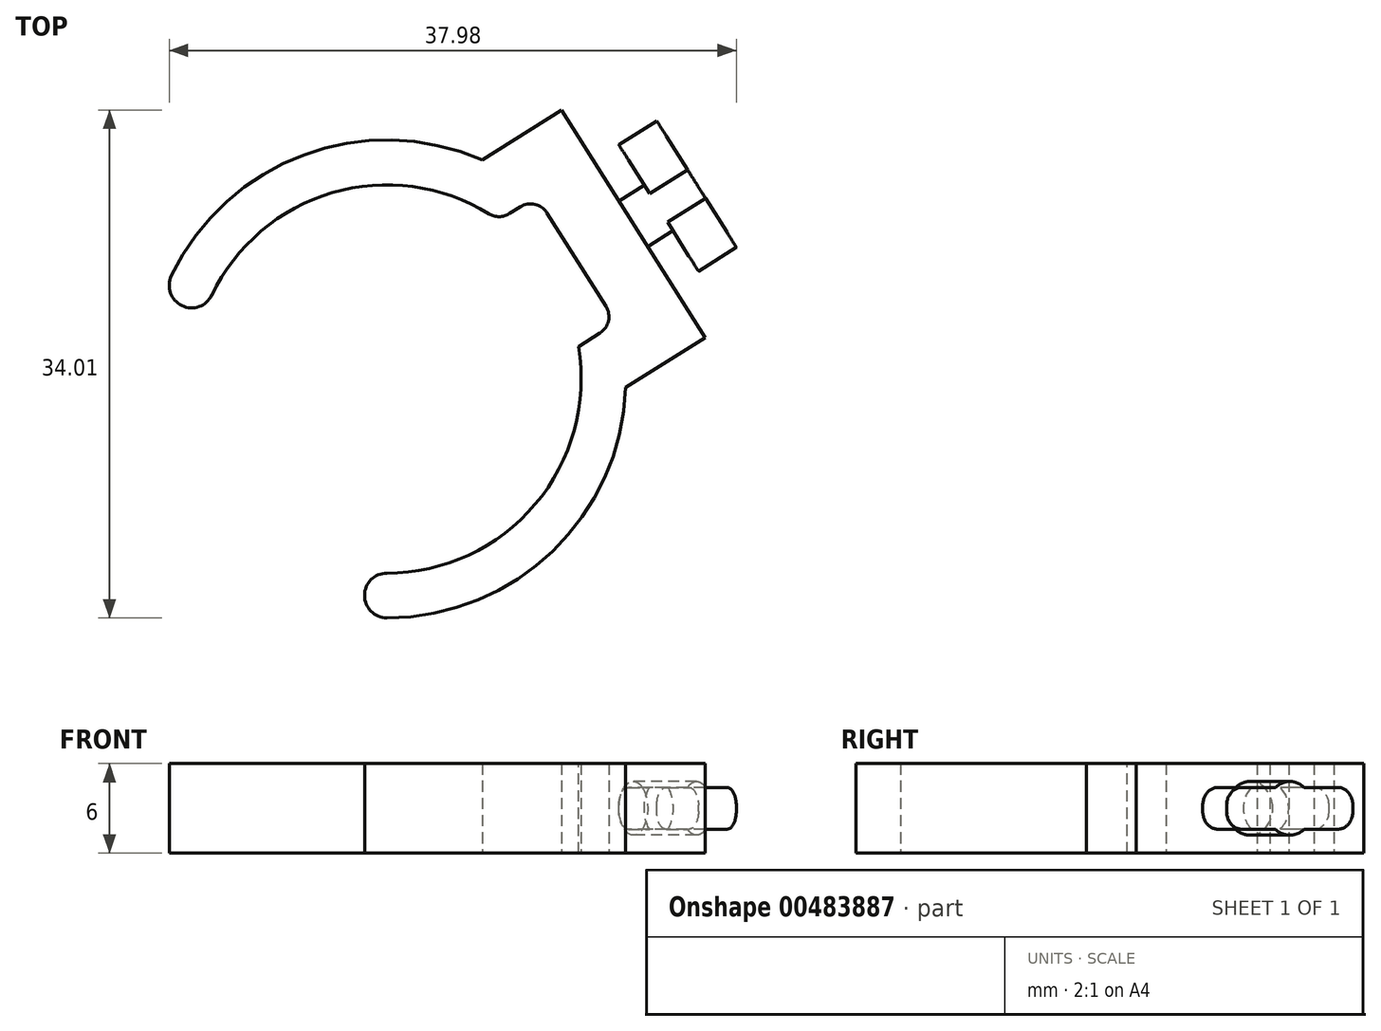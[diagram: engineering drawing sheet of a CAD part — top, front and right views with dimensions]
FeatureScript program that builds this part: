
annotation { "Feature Type Name" : "Feature", "Feature Type Description" : "" }
export const myFeature = defineFeature(function(context is Context, id is Id, definition is map)
    precondition{}
    {
        {
            var Q0;
            Q0=qCreatedBy(makeId("Top.planeOp"),FACE);
            var sketch = newSketch(context, id + "F0", { "sketchPlane" : qUnion([Q0])});
            skArc(sketch, "E0", {"start": v(0, -13) * mm, "mid": v(11, 6.93) * mm, "end": v(-11.72, 5.62) * mm});
            skArc(sketch, "E1.0", {"start": v(0, -16) * mm, "mid": v(13.54, 8.53) * mm, "end": v(-14.43, 6.91) * mm});
            skArc(sketch, "E2", {"start": v(-14.43, 6.91) * mm, "mid": v(-13.73, 4.91) * mm, "end": v(-11.72, 5.62) * mm});
            skArc(sketch, "E3", {"start": v(0, -13) * mm, "mid": v(-1.5, -14.5) * mm, "end": v(0, -16) * mm});
            skLineSegment(sketch, "E4", {"start": v(11, 6.93) * mm, "end": v(15.8, -0.69) * mm});
            skLineSegment(sketch, "E5", {"start": v(15.8, -0.69) * mm, "end": v(21.3, 2.78) * mm});
            skLineSegment(sketch, "E6", {"start": v(21.3, 2.78) * mm, "end": v(11.7, 18) * mm});
            skLineSegment(sketch, "E7", {"start": v(11.7, 18) * mm, "end": v(6.2, 14.54) * mm});
            skLineSegment(sketch, "E8", {"start": v(6.2, 14.54) * mm, "end": v(11, 6.93) * mm});
            skSolve(sketch);
        }
        {
            var Q0;
            {var subQ0=sQuery(id+"F0.wireOp",EDGE,"E3");Q0=makeQuery(id+"F0.imprint","IMPRINT",FACE,{"disambiguationData":[TD([[makeQuery(id+"F0.imprint","IMPRINT",EDGE,{"derivedFrom":subQ0}),1.0]])]});}
            var Q1;
            {var subQ0=sQuery(id+"F0.wireOp",EDGE,"E2");Q1=makeQuery(id+"F0.imprint","IMPRINT",FACE,{"disambiguationData":[TD([[makeQuery(id+"F0.imprint","IMPRINT",EDGE,{"derivedFrom":subQ0}),1.0]])]});}
            var Q2;
            {var subQ0=sQuery(id+"F0.wireOp",EDGE,"E4");var subQ1=sQuery(id+"F0.wireOp",EDGE,"E1.0");var subQ2=makeQuery(id+"F0.imprint","INTERSECT",VERTEX,{"derivedFrom":[subQ1,subQ0]});Q2=makeQuery(id+"F0.imprint","IMPRINT",FACE,{"disambiguationData":[TD([[makeQuery(id+"F0.imprint","IMPRINT",EDGE,{"disambiguationData":[TD([[subQ2,-1.0]])],"derivedFrom":subQ1}),1.0]])]});}
            var Q3;
            {var subQ0=sQuery(id+"F0.wireOp",EDGE,"E5");Q3=makeQuery(id+"F0.imprint","IMPRINT",FACE,{"disambiguationData":[TD([[makeQuery(id+"F0.imprint","IMPRINT",EDGE,{"derivedFrom":subQ0}),1.0]])]});}
            extrude(context, id + "F1", {"entities" : qUnion([Q0, Q1, Q2, Q3]), "depth" : 6 * mm});
        }
        {
            var Q0;
            Q0=makeQuery(id+"F1.opExtrude","SWEPT_FACE",FACE,{"disambiguationData":[OSD([sQuery(id+"F0.wireOp",EDGE,"E6")])]});
            var sketch = newSketch(context, id + "F2", { "sketchPlane" : qUnion([Q0])});
            skCircle(sketch, "E9", {"center": v(0, 3) * mm, "radius": 1.8 * mm});
            skSolve(sketch);
        }
        {
            var Q0;
            Q0=makeQuery(id+"F2.imprint","IMPRINT",FACE,{"disambiguationData":[TD([[makeQuery(id+"F2.imprint","IMPRINT",EDGE,{"derivedFrom":sQuery(id+"F2.wireOp",EDGE,"E9")}),1.0]])]});
            extrude(context, id + "F3", {"entities" : qUnion([Q0]), "operationType" : NewBodyOperationType.ADD, "depth" : 2 * mm});
        }
        {
            var Q0;
            Q0=makeQuery(id+"F3.opExtrude","CAP_FACE",FACE,{"disambiguationData":[OSD([sQuery(id+"F2.wireOp",EDGE,"E9")])],"isStart":false});
            var sketch = newSketch(context, id + "F4", { "sketchPlane" : qUnion([Q0])});
            skLineSegment(sketch, "E10.bottom", {"start": v(5, 1.6) * mm, "end": v(-5, 1.6) * mm});
            skLineSegment(sketch, "E10.top", {"start": v(5, 4.4) * mm, "end": v(-5, 4.4) * mm});
            skLineSegment(sketch, "E10.left", {"start": v(5, 1.6) * mm, "end": v(5, 4.4) * mm});
            skLineSegment(sketch, "E10.right", {"start": v(-5, 1.6) * mm, "end": v(-5, 4.4) * mm});
            skPoint(sketch, "E10.middle", {"position": v(0, 3) * mm});
            skSolve(sketch);
        }
        {
            var Q0;
            {var subQ0=sQuery(id+"F4.wireOp",EDGE,"E10.top");var subQ1=makeQuery(id+"F3.opExtrude","CAP_EDGE",EDGE,{"disambiguationData":[OSD([sQuery(id+"F2.wireOp",EDGE,"E9")])],"isStart":false});var subQ2=makeQuery(id+"F4.imprint","INTERSECT",VERTEX,{"disambiguationData":[OD(0.0)],"derivedFrom":[subQ1,subQ0]});Q0=makeQuery(id+"F4.imprint","IMPRINT",FACE,{"disambiguationData":[TD([[makeQuery(id+"F4.imprint","IMPRINT",EDGE,{"disambiguationData":[TD([[subQ2,-1.0]])],"derivedFrom":subQ0}),-1.0]])]});}
            var Q1;
            {var subQ0=sQuery(id+"F4.wireOp",EDGE,"E10.bottom");var subQ1=makeQuery(id+"F3.opExtrude","CAP_EDGE",EDGE,{"disambiguationData":[OSD([sQuery(id+"F2.wireOp",EDGE,"E9")])],"isStart":false});var subQ2=makeQuery(id+"F4.imprint","INTERSECT",VERTEX,{"disambiguationData":[OD(0.0)],"derivedFrom":[subQ1,subQ0]});Q1=makeQuery(id+"F4.imprint","IMPRINT",FACE,{"disambiguationData":[TD([[makeQuery(id+"F4.imprint","IMPRINT",EDGE,{"disambiguationData":[TD([[subQ2,-1.0]])],"derivedFrom":subQ0}),-1.0]])]});}
            var Q2;
            {var subQ0=sQuery(id+"F4.wireOp",EDGE,"E10.left");Q2=makeQuery(id+"F4.imprint","IMPRINT",FACE,{"disambiguationData":[TD([[makeQuery(id+"F4.imprint","IMPRINT",EDGE,{"derivedFrom":subQ0}),1.0]])]});}
            var Q3;
            {var subQ0=sQuery(id+"F4.wireOp",EDGE,"E10.right");Q3=makeQuery(id+"F4.imprint","IMPRINT",FACE,{"disambiguationData":[TD([[makeQuery(id+"F4.imprint","IMPRINT",EDGE,{"derivedFrom":subQ0}),-1.0]])]});}
            var Q4;
            {var subQ0=sQuery(id+"F4.wireOp",EDGE,"E10.bottom");var subQ1=makeQuery(id+"F3.opExtrude","CAP_EDGE",EDGE,{"disambiguationData":[OSD([sQuery(id+"F2.wireOp",EDGE,"E9")])],"isStart":false});var subQ2=makeQuery(id+"F4.imprint","INTERSECT",VERTEX,{"disambiguationData":[OD(0.0)],"derivedFrom":[subQ1,subQ0]});Q4=makeQuery(id+"F4.imprint","IMPRINT",FACE,{"disambiguationData":[TD([[makeQuery(id+"F4.imprint","IMPRINT",EDGE,{"disambiguationData":[TD([[subQ2,-1.0]])],"derivedFrom":subQ0}),1.0]])]});}
            extrude(context, id + "F5", {"entities" : qUnion([Q0, Q1, Q2, Q3, Q4]), "operationType" : NewBodyOperationType.ADD, "depth" : 3 * mm});
        }
        {
            var Q0;
            Q0=makeQuery(id+"F5.opExtrude","SWEPT_EDGE",EDGE,{"disambiguationData":[OSD([sQuery(id+"F4.wireOp",EDGE,"E10.top"),sQuery(id+"F4.wireOp",EDGE,"E10.right")])]});
            var Q1;
            Q1=makeQuery(id+"F5.opExtrude","SWEPT_EDGE",EDGE,{"disambiguationData":[OSD([sQuery(id+"F4.wireOp",EDGE,"E10.bottom"),sQuery(id+"F4.wireOp",EDGE,"E10.right")])]});
            var Q2;
            Q2=makeQuery(id+"F5.opExtrude","SWEPT_EDGE",EDGE,{"disambiguationData":[OSD([sQuery(id+"F4.wireOp",EDGE,"E10.top"),sQuery(id+"F4.wireOp",EDGE,"E10.left")])]});
            var Q3;
            Q3=makeQuery(id+"F5.opExtrude","SWEPT_EDGE",EDGE,{"disambiguationData":[OSD([sQuery(id+"F4.wireOp",EDGE,"E10.bottom"),sQuery(id+"F4.wireOp",EDGE,"E10.left")])]});
            fillet(context, id + "F6", {"entities" : qUnion([Q0, Q1, Q2, Q3]), "radius" : 1.2 * mm, "tangentPropagation" : true, "allowEdgeOverflow" : false});
        }
        {
            var Q0;
            Q0=makeQuery(id+"F1.opExtrude","CAP_FACE",FACE,{"disambiguationData":[OSD([sQuery(id+"F0.wireOp",EDGE,"E0"),sQuery(id+"F0.wireOp",EDGE,"E1.0"),sQuery(id+"F0.wireOp",EDGE,"E2"),sQuery(id+"F0.wireOp",EDGE,"E3"),sQuery(id+"F0.wireOp",EDGE,"E4"),sQuery(id+"F0.wireOp",EDGE,"E5"),sQuery(id+"F0.wireOp",EDGE,"E6"),sQuery(id+"F0.wireOp",EDGE,"E7"),sQuery(id+"F0.wireOp",EDGE,"E8")])],"isStart":false});
            var sketch = newSketch(context, id + "F7", { "sketchPlane" : qUnion([Q0])});
            skLineSegment(sketch, "E11", {"start": v(16.5, 10.4) * mm, "end": v(11, 6.93) * mm, "construction": true});
            skLineSegment(sketch, "E12", {"start": v(11, 6.93) * mm, "end": v(12.7, 8) * mm});
            skLineSegment(sketch, "E13", {"start": v(12.7, 8) * mm, "end": v(15.36, 3.76) * mm});
            skLineSegment(sketch, "E14", {"start": v(15.36, 3.76) * mm, "end": v(11.97, 1.63) * mm});
            skLineSegment(sketch, "E15", {"start": v(11.97, 1.63) * mm, "end": v(6.64, 10.1) * mm});
            skLineSegment(sketch, "E16", {"start": v(6.64, 10.1) * mm, "end": v(10.03, 12.22) * mm});
            skLineSegment(sketch, "E17", {"start": v(10.03, 12.22) * mm, "end": v(12.7, 8) * mm});
            skSolve(sketch);
        }
        {
            var Q0;
            {var subQ0=sQuery(id+"F7.wireOp",EDGE,"E12");Q0=makeQuery(id+"F7.imprint","IMPRINT",FACE,{"disambiguationData":[TD([[makeQuery(id+"F7.imprint","IMPRINT",EDGE,{"derivedFrom":subQ0}),1.0]])]});}
            var Q1;
            {var subQ0=sQuery(id+"F7.wireOp",EDGE,"E12");Q1=makeQuery(id+"F7.imprint","IMPRINT",FACE,{"disambiguationData":[TD([[makeQuery(id+"F7.imprint","IMPRINT",EDGE,{"derivedFrom":subQ0}),-1.0]])]});}
            extrude(context, id + "F8", {"entities" : qUnion([Q0, Q1]), "operationType" : NewBodyOperationType.REMOVE, "oppositeDirection" : true, "depth" : 6.1 * mm});
        }
        {
            var Q0;
            Q0=makeQuery(id+"F8.boolean.opBoolean","COPY",EDGE,{"derivedFrom":makeQuery(id+"F8.opExtrude","SWEPT_EDGE",EDGE,{"disambiguationData":[OSD([sQuery(id+"F0.wireOp",EDGE,"E0"),sQuery(id+"F7.wireOp",EDGE,"E16")])]})});
            var Q1;
            Q1=makeQuery(id+"F8.boolean.opBoolean","COPY",EDGE,{"derivedFrom":makeQuery(id+"F8.opExtrude","SWEPT_EDGE",EDGE,{"disambiguationData":[OSD([sQuery(id+"F7.wireOp",EDGE,"E16"),sQuery(id+"F7.wireOp",EDGE,"E17")])]})});
            var Q2;
            Q2=makeQuery(id+"F8.boolean.opBoolean","COPY",EDGE,{"derivedFrom":makeQuery(id+"F8.opExtrude","SWEPT_EDGE",EDGE,{"disambiguationData":[OSD([sQuery(id+"F0.wireOp",EDGE,"E0"),sQuery(id+"F7.wireOp",EDGE,"E14")])]})});
            var Q3;
            Q3=makeQuery(id+"F8.boolean.opBoolean","COPY",EDGE,{"derivedFrom":makeQuery(id+"F8.opExtrude","SWEPT_EDGE",EDGE,{"disambiguationData":[OSD([sQuery(id+"F7.wireOp",EDGE,"E13"),sQuery(id+"F7.wireOp",EDGE,"E14")])]})});
            fillet(context, id + "F9", {"entities" : qUnion([Q0, Q1, Q2, Q3]), "radius" : 1.3 * mm, "tangentPropagation" : true, "allowEdgeOverflow" : false});
        }
    });
